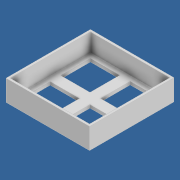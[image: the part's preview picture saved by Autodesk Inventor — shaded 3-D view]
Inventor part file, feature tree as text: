
AUTODESK INVENTOR PART (.ipt)
format: ipt  version: 2020 (Build 240168000, 168)  size: 141,312 bytes
history: native  units: in
note: dims shown in document units (in); Inventor stores cm internally (conversion verified against a paired STEP export)
features: extrude x3, sketch x3
ambient origin geometry x8: Origin, YZ Plane, XZ Plane, XY Plane, X Axis, Y Axis, Z Axis, Center Point
bodies: Solid1 (feature_tree)
feature tree (6):
  extrude  "Extrusion1"  Depth=1.5866in
  extrude  "Extrusion7"  Depth=1.4921in
  extrude  "Extrusion8"  Depth=0.0394in
  sketch  "Sketch1"  dims[d0=1.5709in d1=1.5866in]
  sketch  "Sketch8"  dims[d2=0.3937in d3=0.0in d61=1.4921in]
  sketch  "Sketch9"  dims[d62=1.5079in d63=0.0394in d64=0.0394in d65=0.3346in d66=0.0in d67=0.5512in d68=0.5591in d69=0.0965in d70=0.0965in d71=0.5512in d72=0.5591in d73=0.1969in d74=0.5512in d75=0.5591in d76=0.1969in d77=0.0965in d78=0.5512in d79=0.5591in d80=0.1969in d81=0.1969in d82=0.3346in d83=0.0in]
